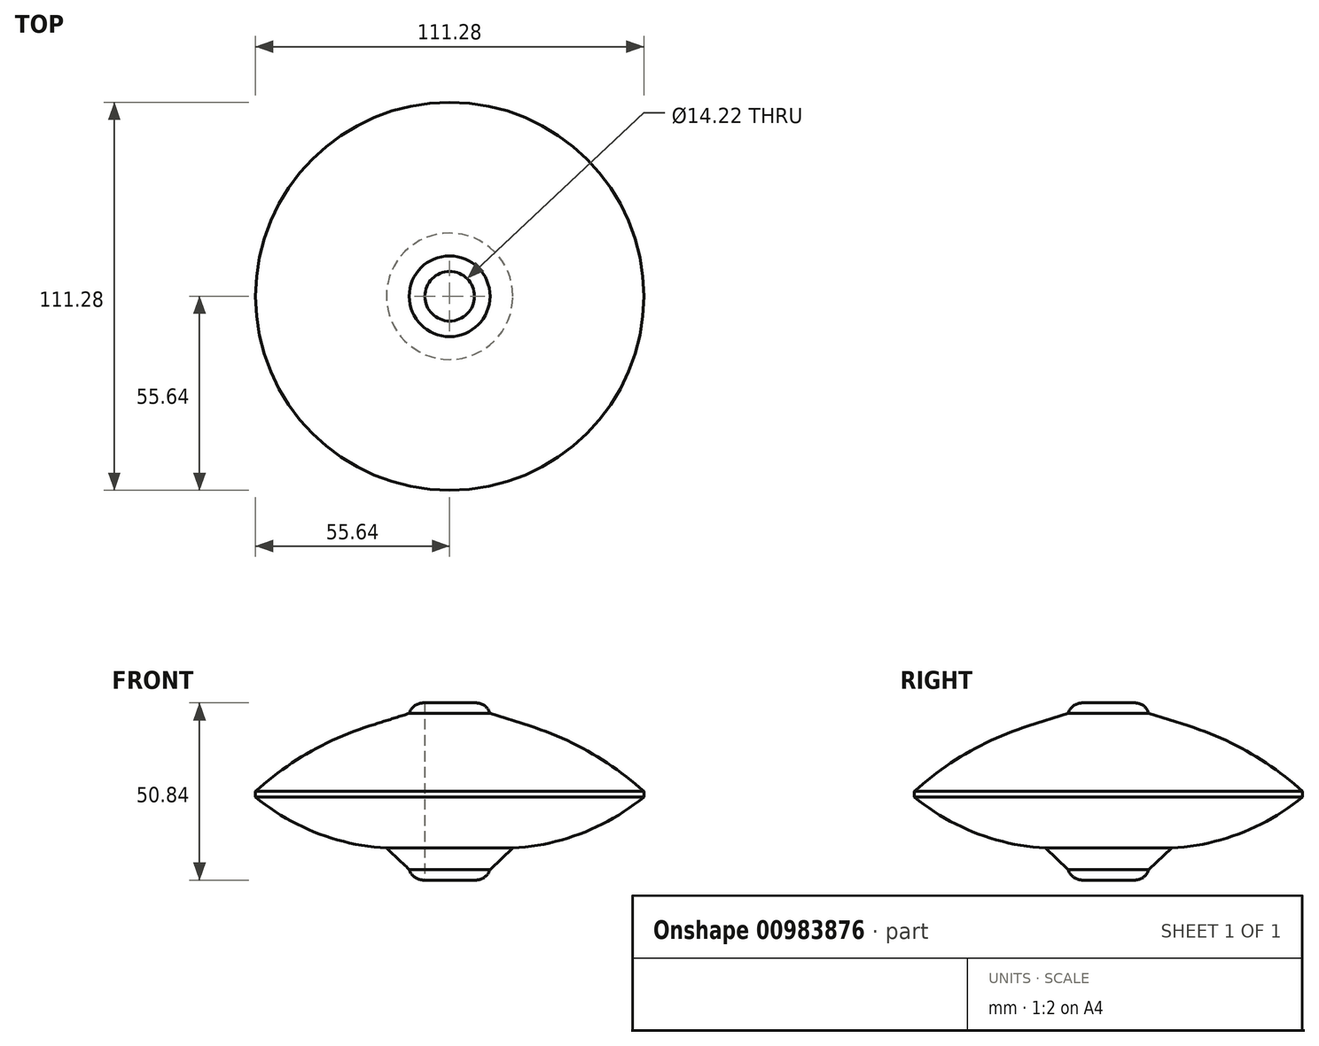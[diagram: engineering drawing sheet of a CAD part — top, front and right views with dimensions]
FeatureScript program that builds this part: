
annotation { "Feature Type Name" : "Feature", "Feature Type Description" : "" }
export const myFeature = defineFeature(function(context is Context, id is Id, definition is map)
    precondition{}
    {
        {
            var Q0;
            Q0=qCreatedBy(makeId("Front.planeOp"),FACE);
            var sketch = newSketch(context, id + "F0", { "sketchPlane" : qUnion([Q0])});
            skLineSegment(sketch, "E0", {"start": v(0, 0) * mm, "end": v(7.11, 0) * mm});
            skLineSegment(sketch, "E1", {"start": v(7.11, 0) * mm, "end": v(7.11, 25.4) * mm});
            skArc(sketch, "E2", {"start": v(11.58, 22.4) * mm, "mid": v(9.87, 24.69) * mm, "end": v(7.11, 25.4) * mm});
            skLineSegment(sketch, "E3", {"start": v(11.58, 22.4) * mm, "end": v(22.91, 18.82) * mm});
            skArc(sketch, "E4", {"start": v(55.64, 0) * mm, "mid": v(40.3, 11.19) * mm, "end": v(22.91, 18.82) * mm});
            skLineSegment(sketch, "E5", {"start": v(55.64, 0) * mm, "end": v(55.64, -1.6) * mm});
            skArc(sketch, "E6.MirrorCS", {"start": v(11.58, -22.4) * mm, "mid": v(9.87, -24.69) * mm, "end": v(7.11, -25.4) * mm});
            skLineSegment(sketch, "E7.MirrorCS", {"start": v(7.11, 0) * mm, "end": v(7.11, -25.4) * mm});
            skLineSegment(sketch, "E8", {"start": v(11.58, -22.4) * mm, "end": v(18.12, -16.2) * mm});
            skArc(sketch, "E9", {"start": v(18.12, -16.2) * mm, "mid": v(38.05, -11.92) * mm, "end": v(55.64, -1.6) * mm});
            skLineSegment(sketch, "E10", {"start": v(0, 0) * mm, "end": v(0, 60.73) * mm});
            skSolve(sketch);
        }
        {
            var Q0;
            Q0=makeQuery(id+"F0.imprint","IMPRINT",FACE,{"disambiguationData":[TD([[makeQuery(id+"F0.imprint","IMPRINT",EDGE,{"derivedFrom":sQuery(id+"F0.wireOp",EDGE,"E1")}),-1.0]])]});
            var Q1;
            Q1=sQuery(id+"F0.wireOp",EDGE,"E10");
            revolve(context, id + "F1", {"surfaceOperationType" : NewSurfaceOperationType.NEW, "entities" : qUnion([Q0]), "axis" : qUnion([Q1]), "revolveType" : RevolveType.FULL});
        }
    });
